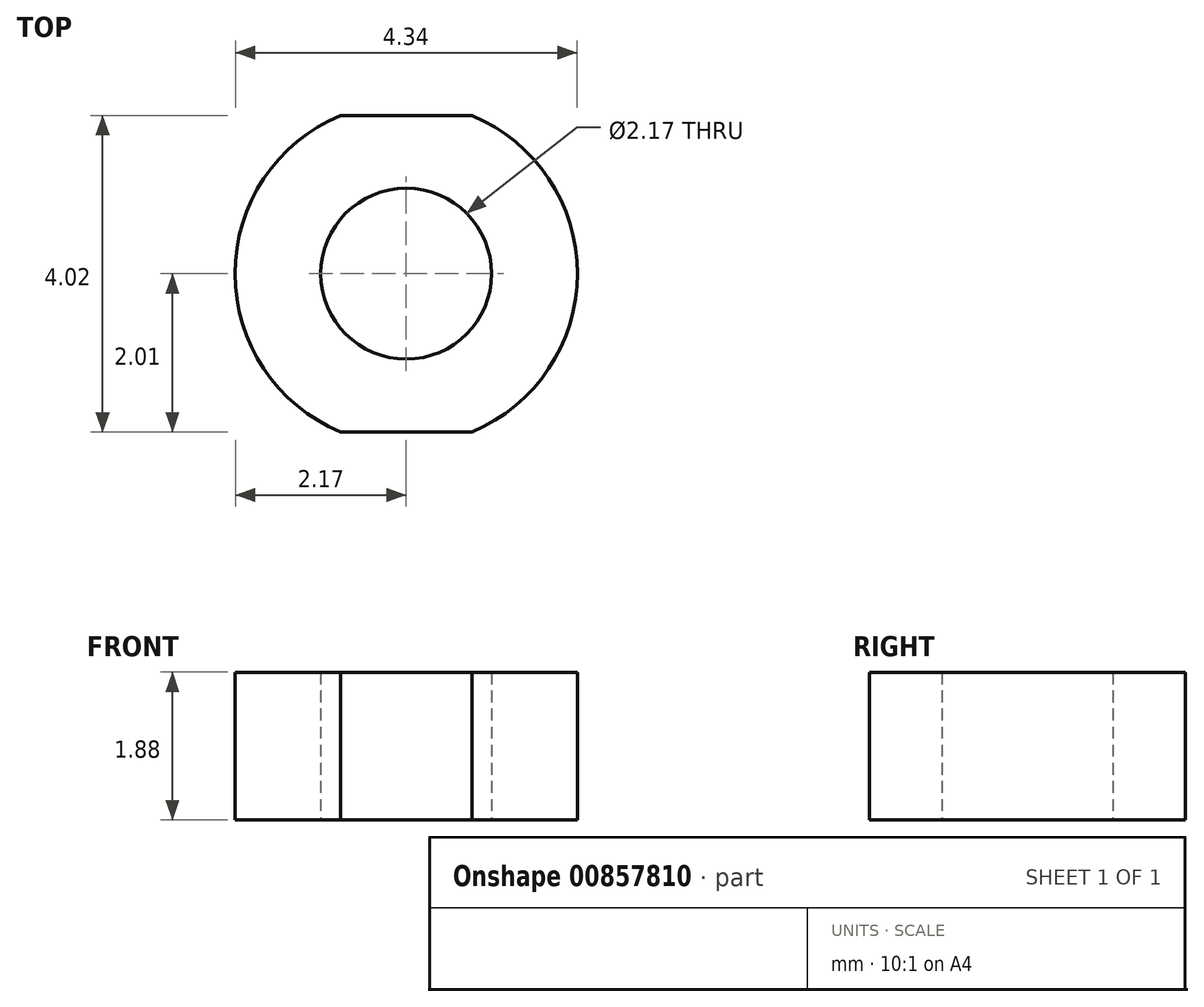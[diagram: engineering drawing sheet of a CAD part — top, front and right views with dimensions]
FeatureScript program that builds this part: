
annotation { "Feature Type Name" : "Feature", "Feature Type Description" : "" }
export const myFeature = defineFeature(function(context is Context, id is Id, definition is map)
    precondition{}
    {
        {
            var Q0;
            Q0=qCreatedBy(makeId("Top.planeOp"),FACE);
            var sketch = newSketch(context, id + "F0", { "sketchPlane" : qUnion([Q0])});
            skCircle(sketch, "E0", {"center": v(0, 0) * mm, "radius": 2.17 * mm});
            skCircle(sketch, "E1", {"center": v(0, 0) * mm, "radius": 1.08 * mm});
            skLineSegment(sketch, "E2", {"start": v(-0.83, 2) * mm, "end": v(0.84, 2) * mm});
            skLineSegment(sketch, "E3.MirrorCS", {"start": v(-0.83, -2) * mm, "end": v(0.84, -2) * mm});
            skSolve(sketch);
        }
        {
            var Q0;
            Q0=makeQuery(id+"F0.imprint","IMPRINT",FACE,{"disambiguationData":[TD([[makeQuery(id+"F0.imprint","IMPRINT",EDGE,{"derivedFrom":sQuery(id+"F0.wireOp",EDGE,"E1")}),-1.0]])]});
            extrude(context, id + "F1", {"entities" : qUnion([Q0]), "depth" : 1.88 * mm, "offsetDistance" : 25 * mm});
        }
    });
